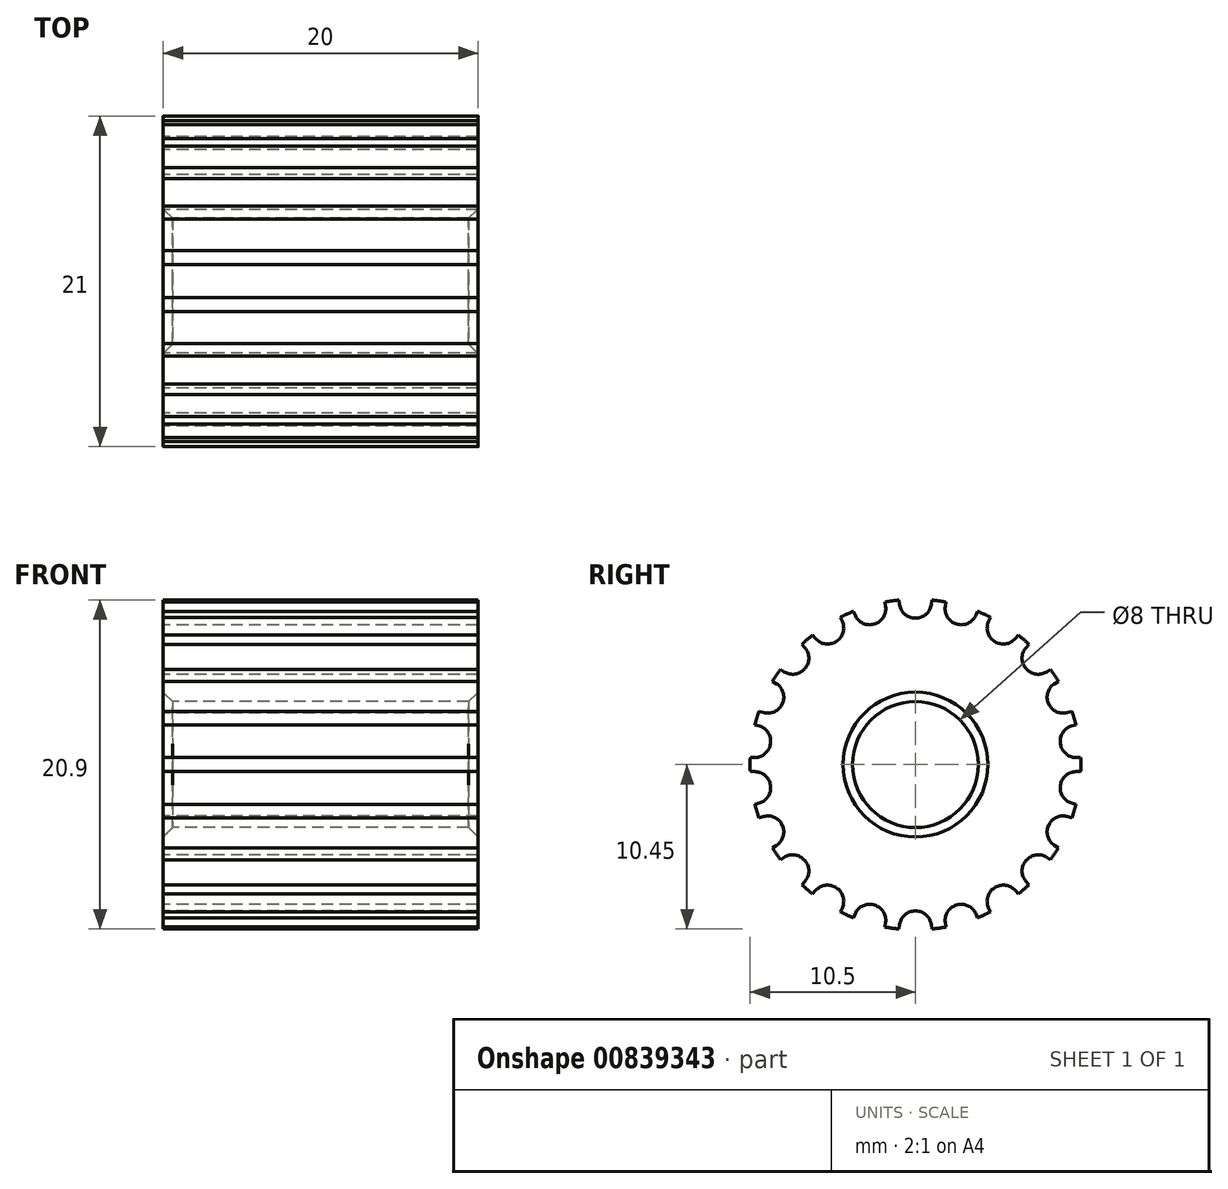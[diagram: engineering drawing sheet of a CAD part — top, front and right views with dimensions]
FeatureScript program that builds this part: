
annotation { "Feature Type Name" : "Feature", "Feature Type Description" : "" }
export const myFeature = defineFeature(function(context is Context, id is Id, definition is map)
    precondition{}
    {
        {
            var Q0;
            Q0=qCreatedBy(makeId("Right.planeOp"),FACE);
            var sketch = newSketch(context, id + "F0", { "sketchPlane" : qUnion([Q0])});
            skCircle(sketch, "E0", {"center": v(0, 0) * mm, "radius": 4 * mm});
            skLineSegment(sketch, "E1", {"start": v(0, 0) * mm, "end": v(0, 10.5) * mm, "construction": true});
            skLineSegment(sketch, "E2.anchor1", {"start": v(0, 0) * mm, "end": v(0, 20.76) * mm, "construction": true});
            skLineSegment(sketch, "E3", {"start": v(-1.5, 10.4) * mm, "end": v(-1.5, 10.4) * mm});
            skLineSegment(sketch, "E4.MirrorCS", {"start": v(1.5, 10.4) * mm, "end": v(1.5, 10.4) * mm});
            skPoint(sketch, "E5", {"position": v(-1.5, 10.4) * mm});
            skPoint(sketch, "E6", {"position": v(1.5, 10.4) * mm});
            skLineSegment(sketch, "E7.trimOffspring", {"start": v(0, 10.5) * mm, "end": v(0, 20.76) * mm, "construction": true});
            skLineSegment(sketch, "E8", {"start": v(-1.05, 10.45) * mm, "end": v(-1, 10.16) * mm});
            skPoint(sketch, "E9", {"position": v(-1.32, 9.2) * mm});
            skArc(sketch, "E10", {"start": v(0.01, 9.3) * mm, "mid": v(0, 9.3) * mm, "end": v(-0.01, 9.3) * mm});
            skArc(sketch, "E11.filletArc", {"start": v(-1, 10.16) * mm, "mid": v(-0.67, 9.54) * mm, "end": v(-0.01, 9.3) * mm});
            skLineSegment(sketch, "E12.MirrorCS", {"start": v(1.05, 10.45) * mm, "end": v(1, 10.16) * mm});
            skArc(sketch, "E13.MirrorCS", {"start": v(1, 10.16) * mm, "mid": v(0.67, 9.54) * mm, "end": v(0.01, 9.3) * mm});
            skPoint(sketch, "E14.orphan", {"position": v(-0.57, 3.96) * mm});
            skPoint(sketch, "E15.orphan", {"position": v(0.57, 3.96) * mm});
            skArc(sketch, "E16", {"start": v(-1.05, 10.45) * mm, "mid": v(-1.5, 10.4) * mm, "end": v(-1.94, 10.32) * mm});
            skLineSegment(sketch, "E17.1.0", {"start": v(-3.95, 9.73) * mm, "end": v(-3.83, 9.46) * mm});
            skArc(sketch, "E17.1.1", {"start": v(-3.83, 9.46) * mm, "mid": v(-3.33, 8.97) * mm, "end": v(-2.63, 8.92) * mm});
            skArc(sketch, "E17.1.2", {"start": v(-2.6, 8.93) * mm, "mid": v(-2.62, 8.92) * mm, "end": v(-2.63, 8.92) * mm});
            skArc(sketch, "E17.1.3", {"start": v(-1.9, 10.03) * mm, "mid": v(-2.05, 9.35) * mm, "end": v(-2.6, 8.93) * mm});
            skLineSegment(sketch, "E17.1.4", {"start": v(-1.94, 10.32) * mm, "end": v(-1.9, 10.03) * mm});
            skLineSegment(sketch, "E17.2.0", {"start": v(-6.53, 8.22) * mm, "end": v(-6.34, 8) * mm});
            skArc(sketch, "E17.2.1", {"start": v(-6.34, 8) * mm, "mid": v(-5.72, 7.67) * mm, "end": v(-5.04, 7.82) * mm});
            skArc(sketch, "E17.2.2", {"start": v(-5.02, 7.83) * mm, "mid": v(-5.03, 7.82) * mm, "end": v(-5.04, 7.82) * mm});
            skArc(sketch, "E17.2.3", {"start": v(-4.65, 9.09) * mm, "mid": v(-4.6, 8.4) * mm, "end": v(-5.02, 7.83) * mm});
            skLineSegment(sketch, "E17.2.4", {"start": v(-4.77, 9.36) * mm, "end": v(-4.65, 9.09) * mm});
            skLineSegment(sketch, "E17.3.0", {"start": v(-8.58, 6.05) * mm, "end": v(-8.34, 5.9) * mm});
            skArc(sketch, "E17.3.1", {"start": v(-8.34, 5.9) * mm, "mid": v(-7.65, 5.74) * mm, "end": v(-7.04, 6.08) * mm});
            skArc(sketch, "E17.3.2", {"start": v(-7.02, 6.1) * mm, "mid": v(-7.03, 6.1) * mm, "end": v(-7.04, 6.08) * mm});
            skArc(sketch, "E17.3.3", {"start": v(-7.02, 7.41) * mm, "mid": v(-6.77, 6.76) * mm, "end": v(-7.02, 6.1) * mm});
            skLineSegment(sketch, "E17.3.4", {"start": v(-7.2, 7.63) * mm, "end": v(-7.02, 7.41) * mm});
            skLineSegment(sketch, "E17.4.0", {"start": v(-9.94, 3.39) * mm, "end": v(-9.66, 3.3) * mm});
            skArc(sketch, "E17.4.1", {"start": v(-9.66, 3.3) * mm, "mid": v(-8.96, 3.35) * mm, "end": v(-8.47, 3.85) * mm});
            skArc(sketch, "E17.4.2", {"start": v(-8.45, 3.88) * mm, "mid": v(-8.46, 3.86) * mm, "end": v(-8.47, 3.85) * mm});
            skArc(sketch, "E17.4.3", {"start": v(-8.82, 5.13) * mm, "mid": v(-8.4, 4.57) * mm, "end": v(-8.45, 3.88) * mm});
            skLineSegment(sketch, "E17.4.4", {"start": v(-9.07, 5.3) * mm, "end": v(-8.82, 5.13) * mm});
            skLineSegment(sketch, "E17.5.0", {"start": v(-10.5, 0.45) * mm, "end": v(-10.2, 0.45) * mm});
            skArc(sketch, "E17.5.1", {"start": v(-10.2, 0.45) * mm, "mid": v(-9.54, 0.7) * mm, "end": v(-9.2, 1.3) * mm});
            skArc(sketch, "E17.5.2", {"start": v(-9.2, 1.34) * mm, "mid": v(-9.2, 1.32) * mm, "end": v(-9.2, 1.3) * mm});
            skArc(sketch, "E17.5.3", {"start": v(-9.91, 2.44) * mm, "mid": v(-9.35, 2.02) * mm, "end": v(-9.2, 1.34) * mm});
            skLineSegment(sketch, "E17.5.4", {"start": v(-10.2, 2.52) * mm, "end": v(-9.91, 2.44) * mm});
            skLineSegment(sketch, "E17.6.0", {"start": v(-10.2, -2.52) * mm, "end": v(-9.91, -2.44) * mm});
            skArc(sketch, "E17.6.1", {"start": v(-9.91, -2.44) * mm, "mid": v(-9.35, -2.02) * mm, "end": v(-9.2, -1.34) * mm});
            skArc(sketch, "E17.6.2", {"start": v(-9.2, -1.3) * mm, "mid": v(-9.2, -1.32) * mm, "end": v(-9.2, -1.34) * mm});
            skArc(sketch, "E17.6.3", {"start": v(-10.2, -0.45) * mm, "mid": v(-9.54, -0.7) * mm, "end": v(-9.2, -1.3) * mm});
            skLineSegment(sketch, "E17.6.4", {"start": v(-10.5, -0.45) * mm, "end": v(-10.2, -0.45) * mm});
            skLineSegment(sketch, "E17.7.0", {"start": v(-9.07, -5.3) * mm, "end": v(-8.82, -5.13) * mm});
            skArc(sketch, "E17.7.1", {"start": v(-8.82, -5.13) * mm, "mid": v(-8.4, -4.57) * mm, "end": v(-8.45, -3.88) * mm});
            skArc(sketch, "E17.7.2", {"start": v(-8.47, -3.85) * mm, "mid": v(-8.46, -3.86) * mm, "end": v(-8.45, -3.88) * mm});
            skArc(sketch, "E17.7.3", {"start": v(-9.66, -3.3) * mm, "mid": v(-8.96, -3.35) * mm, "end": v(-8.47, -3.85) * mm});
            skLineSegment(sketch, "E17.7.4", {"start": v(-9.94, -3.39) * mm, "end": v(-9.66, -3.3) * mm});
            skLineSegment(sketch, "E17.8.0", {"start": v(-7.2, -7.63) * mm, "end": v(-7.02, -7.41) * mm});
            skArc(sketch, "E17.8.1", {"start": v(-7.02, -7.41) * mm, "mid": v(-6.77, -6.76) * mm, "end": v(-7.02, -6.1) * mm});
            skArc(sketch, "E17.8.2", {"start": v(-7.04, -6.08) * mm, "mid": v(-7.03, -6.1) * mm, "end": v(-7.02, -6.1) * mm});
            skArc(sketch, "E17.8.3", {"start": v(-8.34, -5.9) * mm, "mid": v(-7.65, -5.74) * mm, "end": v(-7.04, -6.08) * mm});
            skLineSegment(sketch, "E17.8.4", {"start": v(-8.58, -6.05) * mm, "end": v(-8.34, -5.9) * mm});
            skLineSegment(sketch, "E17.9.0", {"start": v(-4.77, -9.36) * mm, "end": v(-4.65, -9.09) * mm});
            skArc(sketch, "E17.9.1", {"start": v(-4.65, -9.09) * mm, "mid": v(-4.6, -8.4) * mm, "end": v(-5.02, -7.83) * mm});
            skArc(sketch, "E17.9.2", {"start": v(-5.04, -7.82) * mm, "mid": v(-5.03, -7.82) * mm, "end": v(-5.02, -7.83) * mm});
            skArc(sketch, "E17.9.3", {"start": v(-6.34, -8) * mm, "mid": v(-5.72, -7.67) * mm, "end": v(-5.04, -7.82) * mm});
            skLineSegment(sketch, "E17.9.4", {"start": v(-6.53, -8.22) * mm, "end": v(-6.34, -8) * mm});
            skLineSegment(sketch, "E17.10.0", {"start": v(-1.94, -10.32) * mm, "end": v(-1.9, -10.03) * mm});
            skArc(sketch, "E17.10.1", {"start": v(-1.9, -10.03) * mm, "mid": v(-2.05, -9.35) * mm, "end": v(-2.6, -8.93) * mm});
            skArc(sketch, "E17.10.2", {"start": v(-2.63, -8.92) * mm, "mid": v(-2.62, -8.92) * mm, "end": v(-2.6, -8.93) * mm});
            skArc(sketch, "E17.10.3", {"start": v(-3.83, -9.46) * mm, "mid": v(-3.33, -8.97) * mm, "end": v(-2.63, -8.92) * mm});
            skLineSegment(sketch, "E17.10.4", {"start": v(-3.95, -9.73) * mm, "end": v(-3.83, -9.46) * mm});
            skLineSegment(sketch, "E17.11.0", {"start": v(1.05, -10.45) * mm, "end": v(1, -10.16) * mm});
            skArc(sketch, "E17.11.1", {"start": v(1, -10.16) * mm, "mid": v(0.67, -9.54) * mm, "end": v(0.01, -9.3) * mm});
            skArc(sketch, "E17.11.2", {"start": v(-0.01, -9.3) * mm, "mid": v(0, -9.3) * mm, "end": v(0.01, -9.3) * mm});
            skArc(sketch, "E17.11.3", {"start": v(-1, -10.16) * mm, "mid": v(-0.67, -9.54) * mm, "end": v(-0.01, -9.3) * mm});
            skLineSegment(sketch, "E17.11.4", {"start": v(-1.05, -10.45) * mm, "end": v(-1, -10.16) * mm});
            skLineSegment(sketch, "E17.12.0", {"start": v(3.95, -9.73) * mm, "end": v(3.83, -9.46) * mm});
            skArc(sketch, "E17.12.1", {"start": v(3.83, -9.46) * mm, "mid": v(3.33, -8.97) * mm, "end": v(2.63, -8.92) * mm});
            skArc(sketch, "E17.12.2", {"start": v(2.6, -8.93) * mm, "mid": v(2.62, -8.92) * mm, "end": v(2.63, -8.92) * mm});
            skArc(sketch, "E17.12.3", {"start": v(1.9, -10.03) * mm, "mid": v(2.05, -9.35) * mm, "end": v(2.6, -8.93) * mm});
            skLineSegment(sketch, "E17.12.4", {"start": v(1.94, -10.32) * mm, "end": v(1.9, -10.03) * mm});
            skLineSegment(sketch, "E17.13.0", {"start": v(6.53, -8.22) * mm, "end": v(6.34, -8) * mm});
            skArc(sketch, "E17.13.1", {"start": v(6.34, -8) * mm, "mid": v(5.72, -7.67) * mm, "end": v(5.04, -7.82) * mm});
            skArc(sketch, "E17.13.2", {"start": v(5.02, -7.83) * mm, "mid": v(5.03, -7.82) * mm, "end": v(5.04, -7.82) * mm});
            skArc(sketch, "E17.13.3", {"start": v(4.65, -9.09) * mm, "mid": v(4.6, -8.4) * mm, "end": v(5.02, -7.83) * mm});
            skLineSegment(sketch, "E17.13.4", {"start": v(4.77, -9.36) * mm, "end": v(4.65, -9.09) * mm});
            skLineSegment(sketch, "E17.14.0", {"start": v(8.58, -6.05) * mm, "end": v(8.34, -5.9) * mm});
            skArc(sketch, "E17.14.1", {"start": v(8.34, -5.9) * mm, "mid": v(7.65, -5.74) * mm, "end": v(7.04, -6.08) * mm});
            skArc(sketch, "E17.14.2", {"start": v(7.02, -6.1) * mm, "mid": v(7.03, -6.1) * mm, "end": v(7.04, -6.08) * mm});
            skArc(sketch, "E17.14.3", {"start": v(7.02, -7.41) * mm, "mid": v(6.77, -6.76) * mm, "end": v(7.02, -6.1) * mm});
            skLineSegment(sketch, "E17.14.4", {"start": v(7.2, -7.63) * mm, "end": v(7.02, -7.41) * mm});
            skLineSegment(sketch, "E17.15.0", {"start": v(9.94, -3.39) * mm, "end": v(9.66, -3.3) * mm});
            skArc(sketch, "E17.15.1", {"start": v(9.66, -3.3) * mm, "mid": v(8.96, -3.35) * mm, "end": v(8.47, -3.85) * mm});
            skArc(sketch, "E17.15.2", {"start": v(8.45, -3.88) * mm, "mid": v(8.46, -3.86) * mm, "end": v(8.47, -3.85) * mm});
            skArc(sketch, "E17.15.3", {"start": v(8.82, -5.13) * mm, "mid": v(8.4, -4.57) * mm, "end": v(8.45, -3.88) * mm});
            skLineSegment(sketch, "E17.15.4", {"start": v(9.07, -5.3) * mm, "end": v(8.82, -5.13) * mm});
            skLineSegment(sketch, "E17.16.0", {"start": v(10.5, -0.45) * mm, "end": v(10.2, -0.45) * mm});
            skArc(sketch, "E17.16.1", {"start": v(10.2, -0.45) * mm, "mid": v(9.54, -0.7) * mm, "end": v(9.2, -1.3) * mm});
            skArc(sketch, "E17.16.2", {"start": v(9.2, -1.34) * mm, "mid": v(9.2, -1.32) * mm, "end": v(9.2, -1.3) * mm});
            skArc(sketch, "E17.16.3", {"start": v(9.91, -2.44) * mm, "mid": v(9.35, -2.02) * mm, "end": v(9.2, -1.34) * mm});
            skLineSegment(sketch, "E17.16.4", {"start": v(10.2, -2.52) * mm, "end": v(9.91, -2.44) * mm});
            skLineSegment(sketch, "E17.17.0", {"start": v(10.2, 2.52) * mm, "end": v(9.91, 2.44) * mm});
            skArc(sketch, "E17.17.1", {"start": v(9.91, 2.44) * mm, "mid": v(9.35, 2.02) * mm, "end": v(9.2, 1.34) * mm});
            skArc(sketch, "E17.17.2", {"start": v(9.2, 1.3) * mm, "mid": v(9.2, 1.32) * mm, "end": v(9.2, 1.34) * mm});
            skArc(sketch, "E17.17.3", {"start": v(10.2, 0.45) * mm, "mid": v(9.54, 0.7) * mm, "end": v(9.2, 1.3) * mm});
            skLineSegment(sketch, "E17.17.4", {"start": v(10.5, 0.45) * mm, "end": v(10.2, 0.45) * mm});
            skLineSegment(sketch, "E17.18.0", {"start": v(9.07, 5.3) * mm, "end": v(8.82, 5.13) * mm});
            skArc(sketch, "E17.18.1", {"start": v(8.82, 5.13) * mm, "mid": v(8.4, 4.57) * mm, "end": v(8.45, 3.88) * mm});
            skArc(sketch, "E17.18.2", {"start": v(8.47, 3.85) * mm, "mid": v(8.46, 3.86) * mm, "end": v(8.45, 3.88) * mm});
            skArc(sketch, "E17.18.3", {"start": v(9.66, 3.3) * mm, "mid": v(8.96, 3.35) * mm, "end": v(8.47, 3.85) * mm});
            skLineSegment(sketch, "E17.18.4", {"start": v(9.94, 3.39) * mm, "end": v(9.66, 3.3) * mm});
            skLineSegment(sketch, "E17.19.0", {"start": v(7.2, 7.63) * mm, "end": v(7.02, 7.41) * mm});
            skArc(sketch, "E17.19.1", {"start": v(7.02, 7.41) * mm, "mid": v(6.77, 6.76) * mm, "end": v(7.02, 6.1) * mm});
            skArc(sketch, "E17.19.2", {"start": v(7.04, 6.08) * mm, "mid": v(7.03, 6.1) * mm, "end": v(7.02, 6.1) * mm});
            skArc(sketch, "E17.19.3", {"start": v(8.34, 5.9) * mm, "mid": v(7.65, 5.74) * mm, "end": v(7.04, 6.08) * mm});
            skLineSegment(sketch, "E17.19.4", {"start": v(8.58, 6.05) * mm, "end": v(8.34, 5.9) * mm});
            skLineSegment(sketch, "E17.20.0", {"start": v(4.77, 9.36) * mm, "end": v(4.65, 9.09) * mm});
            skArc(sketch, "E17.20.1", {"start": v(4.65, 9.09) * mm, "mid": v(4.6, 8.4) * mm, "end": v(5.02, 7.83) * mm});
            skArc(sketch, "E17.20.2", {"start": v(5.04, 7.82) * mm, "mid": v(5.03, 7.82) * mm, "end": v(5.02, 7.83) * mm});
            skArc(sketch, "E17.20.3", {"start": v(6.34, 8) * mm, "mid": v(5.72, 7.67) * mm, "end": v(5.04, 7.82) * mm});
            skLineSegment(sketch, "E17.20.4", {"start": v(6.53, 8.22) * mm, "end": v(6.34, 8) * mm});
            skLineSegment(sketch, "E17.21.0", {"start": v(1.94, 10.32) * mm, "end": v(1.9, 10.03) * mm});
            skArc(sketch, "E17.21.1", {"start": v(1.9, 10.03) * mm, "mid": v(2.05, 9.35) * mm, "end": v(2.6, 8.93) * mm});
            skArc(sketch, "E17.21.2", {"start": v(2.63, 8.92) * mm, "mid": v(2.62, 8.92) * mm, "end": v(2.6, 8.93) * mm});
            skArc(sketch, "E17.21.3", {"start": v(3.83, 9.46) * mm, "mid": v(3.33, 8.97) * mm, "end": v(2.63, 8.92) * mm});
            skLineSegment(sketch, "E17.21.4", {"start": v(3.95, 9.73) * mm, "end": v(3.83, 9.46) * mm});
            skArc(sketch, "E18.trimOffspring", {"start": v(1.94, 10.32) * mm, "mid": v(1.5, 10.4) * mm, "end": v(1.05, 10.45) * mm});
            skArc(sketch, "E19.trimOffspring", {"start": v(4.77, 9.36) * mm, "mid": v(4.36, 9.55) * mm, "end": v(3.95, 9.73) * mm});
            skArc(sketch, "E20.trimOffspring", {"start": v(7.2, 7.63) * mm, "mid": v(6.88, 7.94) * mm, "end": v(6.53, 8.22) * mm});
            skArc(sketch, "E21.trimOffspring", {"start": v(9.07, 5.3) * mm, "mid": v(8.83, 5.68) * mm, "end": v(8.58, 6.05) * mm});
            skArc(sketch, "E22.trimOffspring", {"start": v(10.2, 2.52) * mm, "mid": v(10.07, 2.96) * mm, "end": v(9.94, 3.39) * mm});
            skArc(sketch, "E23.trimOffspring", {"start": v(10.5, -0.45) * mm, "mid": v(10.5, 0) * mm, "end": v(10.5, 0.45) * mm});
            skArc(sketch, "E24.trimOffspring", {"start": v(9.94, -3.39) * mm, "mid": v(10.07, -2.96) * mm, "end": v(10.2, -2.52) * mm});
            skArc(sketch, "E25.trimOffspring", {"start": v(8.58, -6.05) * mm, "mid": v(8.83, -5.68) * mm, "end": v(9.07, -5.3) * mm});
            skArc(sketch, "E26.trimOffspring", {"start": v(6.53, -8.22) * mm, "mid": v(6.88, -7.94) * mm, "end": v(7.2, -7.63) * mm});
            skArc(sketch, "E27.trimOffspring", {"start": v(3.95, -9.73) * mm, "mid": v(4.36, -9.55) * mm, "end": v(4.77, -9.36) * mm});
            skArc(sketch, "E28.trimOffspring", {"start": v(1.05, -10.45) * mm, "mid": v(1.5, -10.4) * mm, "end": v(1.94, -10.32) * mm});
            skArc(sketch, "E29.trimOffspring", {"start": v(-1.94, -10.32) * mm, "mid": v(-1.5, -10.4) * mm, "end": v(-1.05, -10.45) * mm});
            skArc(sketch, "E30.trimOffspring", {"start": v(-4.77, -9.36) * mm, "mid": v(-4.36, -9.55) * mm, "end": v(-3.95, -9.73) * mm});
            skArc(sketch, "E31.trimOffspring", {"start": v(-7.2, -7.63) * mm, "mid": v(-6.88, -7.94) * mm, "end": v(-6.53, -8.22) * mm});
            skArc(sketch, "E32.trimOffspring", {"start": v(-9.07, -5.3) * mm, "mid": v(-8.83, -5.68) * mm, "end": v(-8.58, -6.05) * mm});
            skArc(sketch, "E33.trimOffspring", {"start": v(-10.2, -2.52) * mm, "mid": v(-10.07, -2.96) * mm, "end": v(-9.94, -3.39) * mm});
            skArc(sketch, "E34.trimOffspring", {"start": v(-10.5, 0.45) * mm, "mid": v(-10.5, 0) * mm, "end": v(-10.5, -0.45) * mm});
            skArc(sketch, "E35.trimOffspring", {"start": v(-9.94, 3.39) * mm, "mid": v(-10.07, 2.96) * mm, "end": v(-10.2, 2.52) * mm});
            skArc(sketch, "E36.trimOffspring", {"start": v(-8.58, 6.05) * mm, "mid": v(-8.83, 5.68) * mm, "end": v(-9.07, 5.3) * mm});
            skArc(sketch, "E37.trimOffspring", {"start": v(-6.53, 8.22) * mm, "mid": v(-6.88, 7.94) * mm, "end": v(-7.2, 7.63) * mm});
            skArc(sketch, "E38.trimOffspring", {"start": v(-3.95, 9.73) * mm, "mid": v(-4.36, 9.55) * mm, "end": v(-4.77, 9.36) * mm});
            skSolve(sketch);
        }
        {
            var Q0;
            Q0=makeQuery(id+"F0.imprint","IMPRINT",FACE,{"disambiguationData":[TD([[makeQuery(id+"F0.imprint","IMPRINT",EDGE,{"derivedFrom":sQuery(id+"F0.wireOp",EDGE,"0MEXwoFq-VW0W-JoZZ-MDqj-tHZCOfQ7mCeB")}),1.0]])]});
            var Q1;
            Q1=makeQuery(id+"F0.imprint","IMPRINT",FACE,{"disambiguationData":[TD([[makeQuery(id+"F0.imprint","IMPRINT",EDGE,{"derivedFrom":sQuery(id+"F0.wireOp",EDGE,"E0")}),-1.0]])]});
            extrude(context, id + "F1", {"entities" : qUnion([Q0, Q1]), "depth" : 20 * mm, "offsetDistance" : 25 * mm});
        }
        {
            var Q0;
            Q0=makeQuery(id+"F1.opExtrude","CAP_EDGE",EDGE,{"disambiguationData":[OSD([sQuery(id+"F0.wireOp",EDGE,"E0")])],"isStart":false});
            var Q1;
            Q1=makeQuery(id+"F1.opExtrude","CAP_EDGE",EDGE,{"disambiguationData":[OSD([sQuery(id+"F0.wireOp",EDGE,"E0")])],"isStart":true});
            chamfer(context, id + "F2", {"entities" : qUnion([Q0, Q1]), "width" : .6 * mm, "tangentPropagation" : true});
        }
    });
